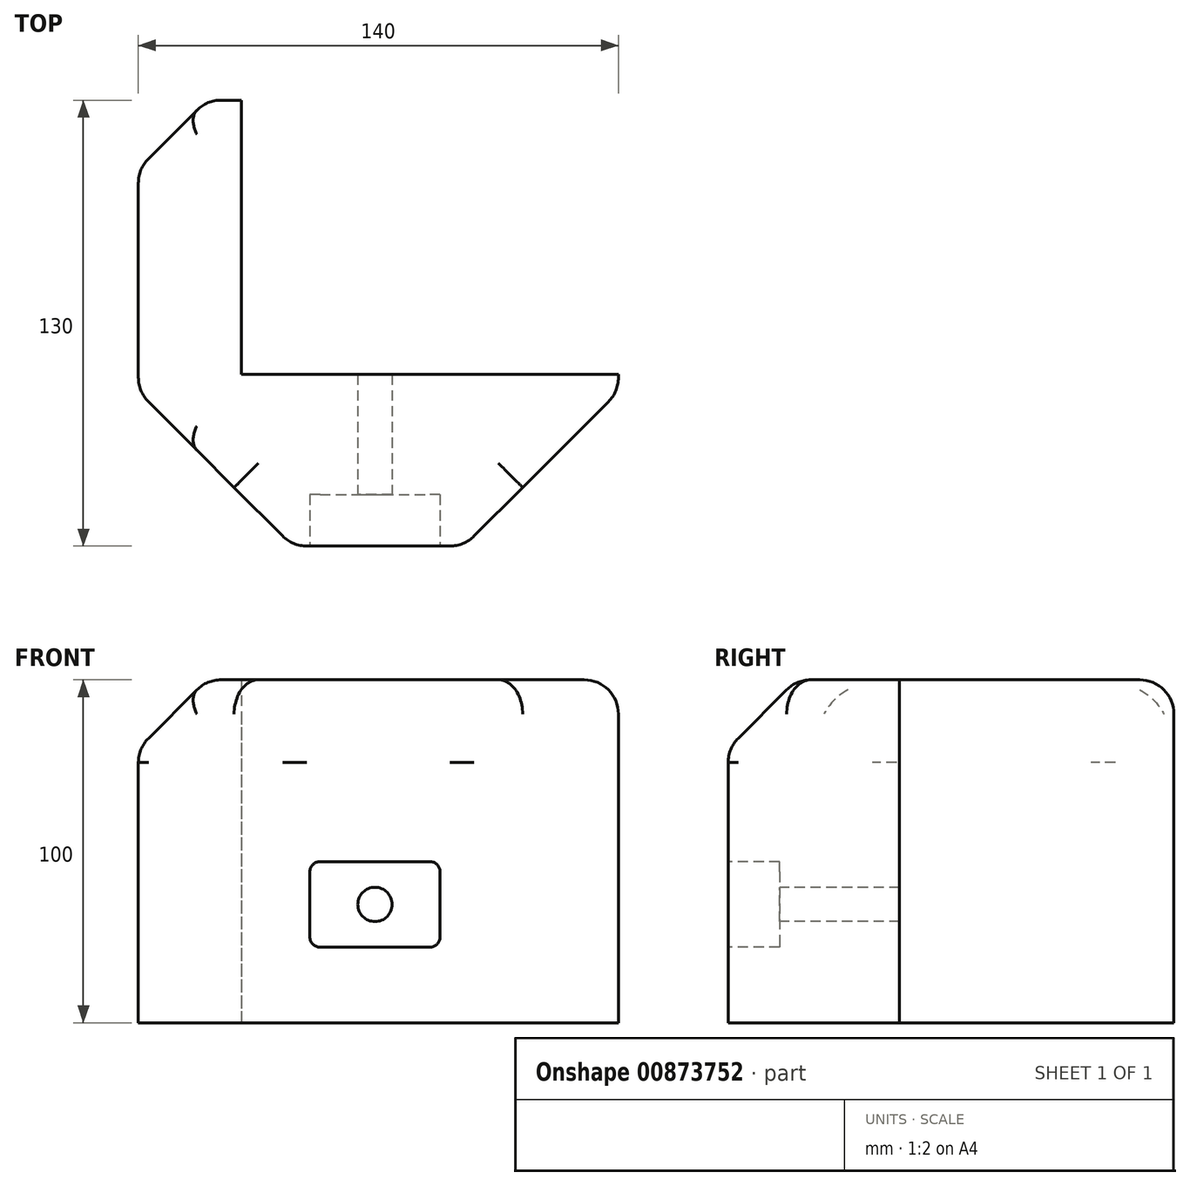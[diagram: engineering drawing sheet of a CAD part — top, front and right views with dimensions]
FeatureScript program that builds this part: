
annotation { "Feature Type Name" : "Feature", "Feature Type Description" : "" }
export const myFeature = defineFeature(function(context is Context, id is Id, definition is map)
    precondition{}
    {
        {
            var Q0;
            Q0=qCreatedBy(makeId("Top.planeOp"),FACE);
            var sketch = newSketch(context, id + "F0", { "sketchPlane" : qUnion([Q0])});
            skLineSegment(sketch, "E0.bottom", {"start": v(-91.77, 41.17) * mm, "end": v(48.23, 41.17) * mm});
            skLineSegment(sketch, "E0.top", {"start": v(-91.77, -8.83) * mm, "end": v(48.23, -8.83) * mm});
            skLineSegment(sketch, "E0.left", {"start": v(-91.77, 41.17) * mm, "end": v(-91.77, -8.83) * mm});
            skLineSegment(sketch, "E0.right", {"start": v(48.23, 41.17) * mm, "end": v(48.23, -8.83) * mm});
            skLineSegment(sketch, "E1.bottom", {"start": v(-91.77, 41.17) * mm, "end": v(-61.77, 41.17) * mm});
            skLineSegment(sketch, "E1.top", {"start": v(-91.77, 121.17) * mm, "end": v(-61.77, 121.17) * mm});
            skLineSegment(sketch, "E1.left", {"start": v(-91.77, 41.17) * mm, "end": v(-91.77, 121.17) * mm});
            skLineSegment(sketch, "E1.right", {"start": v(-61.77, 41.17) * mm, "end": v(-61.77, 121.17) * mm});
            skSolve(sketch);
        }
        {
            var Q0;
            Q0=makeQuery(id+"F0.imprint","IMPRINT",FACE,{"disambiguationData":[TD([[makeQuery(id+"F0.imprint","IMPRINT",EDGE,{"derivedFrom":sQuery(id+"F0.wireOp",EDGE,"E1.top")}),-1.0]])]});
            var Q1;
            Q1=makeQuery(id+"F0.imprint","IMPRINT",FACE,{"disambiguationData":[TD([[makeQuery(id+"F0.imprint","IMPRINT",EDGE,{"derivedFrom":sQuery(id+"F0.wireOp",EDGE,"E0.top")}),1.0]])]});
            extrude(context, id + "F1", {"entities" : qUnion([Q0, Q1]), "depth" : 100 * mm, "offsetDistance" : 25 * mm});
        }
        {
            var Q0;
            Q0=makeQuery(id+"F1.opExtrude","CAP_EDGE",EDGE,{"disambiguationData":[OSD([sQuery(id+"F0.wireOp",EDGE,"E0.top")])],"isStart":false});
            var Q1;
            Q1=makeQuery(id+"F1.opExtrude","CAP_EDGE",EDGE,{"disambiguationData":[OSD([sQuery(id+"F0.wireOp",EDGE,"E0.left"),sQuery(id+"F0.wireOp",EDGE,"E1.left")])],"isStart":false});
            chamfer(context, id + "F2", {"entities" : qUnion([Q0, Q1]), "width" : 20 * mm, "tangentPropagation" : true});
        }
        {
            var Q0;
            Q0=makeQuery(id+"F1.opExtrude","SWEPT_FACE",FACE,{"disambiguationData":[OSD([sQuery(id+"F0.wireOp",EDGE,"E0.top")])]});
            var sketch = newSketch(context, id + "F3", { "sketchPlane" : qUnion([Q0])});
            skLineSegment(sketch, "E2.bottom", {"start": v(-41.77, 47) * mm, "end": v(-3.77, 47) * mm});
            skLineSegment(sketch, "E2.top", {"start": v(-41.77, 22) * mm, "end": v(-3.77, 22) * mm});
            skLineSegment(sketch, "E2.left", {"start": v(-41.77, 47) * mm, "end": v(-41.77, 22) * mm});
            skLineSegment(sketch, "E2.right", {"start": v(-3.77, 47) * mm, "end": v(-3.77, 22) * mm});
            skSolve(sketch);
        }
        {
            var Q0;
            Q0 = qSketchRegion(id + "F3", true);
            extrude(context, id + "F4", {"entities" : qUnion([Q0]), "operationType" : NewBodyOperationType.REMOVE, "oppositeDirection" : true, "depth" : 15 * mm, "offsetDistance" : 25 * mm});
        }
        {
            var Q0;
            Q0=makeQuery(id+"F4.boolean.opBoolean","COPY",EDGE,{"derivedFrom":makeQuery(id+"F4.opExtrude","SWEPT_EDGE",EDGE,{"disambiguationData":[OSD([sQuery(id+"F3.wireOp",EDGE,"E2.bottom"),sQuery(id+"F3.wireOp",EDGE,"E2.left")])]})});
            var Q1;
            Q1=makeQuery(id+"F4.boolean.opBoolean","COPY",EDGE,{"derivedFrom":makeQuery(id+"F4.opExtrude","SWEPT_EDGE",EDGE,{"disambiguationData":[OSD([sQuery(id+"F3.wireOp",EDGE,"E2.top"),sQuery(id+"F3.wireOp",EDGE,"E2.left")])]})});
            var Q2;
            Q2=makeQuery(id+"F4.boolean.opBoolean","COPY",EDGE,{"derivedFrom":makeQuery(id+"F4.opExtrude","SWEPT_EDGE",EDGE,{"disambiguationData":[OSD([sQuery(id+"F3.wireOp",EDGE,"E2.top"),sQuery(id+"F3.wireOp",EDGE,"E2.right")])]})});
            var Q3;
            Q3=makeQuery(id+"F4.boolean.opBoolean","COPY",EDGE,{"derivedFrom":makeQuery(id+"F4.opExtrude","SWEPT_EDGE",EDGE,{"disambiguationData":[OSD([sQuery(id+"F3.wireOp",EDGE,"E2.bottom"),sQuery(id+"F3.wireOp",EDGE,"E2.right")])]})});
            fillet(context, id + "F5", {"entities" : qUnion([Q0, Q1, Q2, Q3]), "radius" : 3 * mm, "tangentPropagation" : true, "allowEdgeOverflow" : false});
        }
        {
            var Q0;
            Q0=makeQuery(id+"F1.opExtrude","SWEPT_EDGE",EDGE,{"disambiguationData":[OSD([sQuery(id+"F0.wireOp",EDGE,"E0.top"),sQuery(id+"F0.wireOp",EDGE,"E0.right")])]});
            var Q1;
            Q1=makeQuery(id+"F1.opExtrude","SWEPT_EDGE",EDGE,{"disambiguationData":[OSD([sQuery(id+"F0.wireOp",EDGE,"E0.top"),sQuery(id+"F0.wireOp",EDGE,"E0.left")])]});
            chamfer(context, id + "F6", {"entities" : qUnion([Q0, Q1]), "width" : 45 * mm, "tangentPropagation" : true});
        }
        {
            var Q0;
            Q0=makeQuery(id+"F1.opExtrude","SWEPT_EDGE",EDGE,{"disambiguationData":[OSD([sQuery(id+"F0.wireOp",EDGE,"E1.top"),sQuery(id+"F0.wireOp",EDGE,"E1.left")])]});
            chamfer(context, id + "F7", {"entities" : qUnion([Q0]), "width" : 20 * mm, "tangentPropagation" : true});
        }
        {
            var Q0;
            {var subQ0=sQuery(id+"F0.wireOp",EDGE,"E0.top");Q0=makeQuery(id+"F6.opChamfer","BLEND_EDGE",EDGE,{"blendedFrom":[makeQuery(id+"F1.opExtrude","SWEPT_EDGE",EDGE,{"disambiguationData":[OSD([subQ0,sQuery(id+"F0.wireOp",EDGE,"E0.left")])]}),makeQuery(id+"F1.opExtrude","SWEPT_FACE",FACE,{"disambiguationData":[OSD([subQ0])]})],"blendedInto":[makeQuery(id+"F1.opExtrude","SWEPT_FACE",FACE,{"disambiguationData":[OSD([subQ0])]})]});}
            var Q1;
            {var subQ0=sQuery(id+"F0.wireOp",EDGE,"E0.top");Q1=makeQuery(id+"F6.opChamfer","BLEND_EDGE",EDGE,{"blendedFrom":[makeQuery(id+"F1.opExtrude","SWEPT_EDGE",EDGE,{"disambiguationData":[OSD([subQ0,sQuery(id+"F0.wireOp",EDGE,"E0.right")])]}),makeQuery(id+"F1.opExtrude","SWEPT_FACE",FACE,{"disambiguationData":[OSD([subQ0])]})],"blendedInto":[makeQuery(id+"F1.opExtrude","SWEPT_FACE",FACE,{"disambiguationData":[OSD([subQ0])]})]});}
            var Q2;
            {var subQ0=sQuery(id+"F0.wireOp",EDGE,"E0.right");Q2=makeQuery(id+"F6.opChamfer","BLEND_EDGE",EDGE,{"blendedFrom":[makeQuery(id+"F1.opExtrude","SWEPT_EDGE",EDGE,{"disambiguationData":[OSD([sQuery(id+"F0.wireOp",EDGE,"E0.top"),subQ0])]}),makeQuery(id+"F1.opExtrude","SWEPT_FACE",FACE,{"disambiguationData":[OSD([subQ0])]})],"blendedInto":[makeQuery(id+"F1.opExtrude","SWEPT_FACE",FACE,{"disambiguationData":[OSD([subQ0])]})]});}
            var Q3;
            {var subQ0=sQuery(id+"F0.wireOp",EDGE,"E0.left");Q3=makeQuery(id+"F6.opChamfer","BLEND_EDGE",EDGE,{"blendedFrom":[makeQuery(id+"F1.opExtrude","SWEPT_EDGE",EDGE,{"disambiguationData":[OSD([sQuery(id+"F0.wireOp",EDGE,"E0.top"),subQ0])]}),makeQuery(id+"F1.opExtrude","SWEPT_FACE",FACE,{"disambiguationData":[OSD([subQ0,sQuery(id+"F0.wireOp",EDGE,"E1.left")])]})],"blendedInto":[makeQuery(id+"F1.opExtrude","SWEPT_FACE",FACE,{"disambiguationData":[OSD([subQ0,sQuery(id+"F0.wireOp",EDGE,"E1.left")])]})]});}
            var Q4;
            {var subQ0=sQuery(id+"F0.wireOp",EDGE,"E1.left");Q4=makeQuery(id+"F7.opChamfer","BLEND_EDGE",EDGE,{"blendedFrom":[makeQuery(id+"F1.opExtrude","SWEPT_EDGE",EDGE,{"disambiguationData":[OSD([sQuery(id+"F0.wireOp",EDGE,"E1.top"),subQ0])]}),makeQuery(id+"F1.opExtrude","SWEPT_FACE",FACE,{"disambiguationData":[OSD([sQuery(id+"F0.wireOp",EDGE,"E0.left"),subQ0])]})],"blendedInto":[makeQuery(id+"F1.opExtrude","SWEPT_FACE",FACE,{"disambiguationData":[OSD([sQuery(id+"F0.wireOp",EDGE,"E0.left"),subQ0])]})]});}
            var Q5;
            {var subQ0=sQuery(id+"F0.wireOp",EDGE,"E1.top");Q5=makeQuery(id+"F7.opChamfer","BLEND_EDGE",EDGE,{"blendedFrom":[makeQuery(id+"F1.opExtrude","SWEPT_EDGE",EDGE,{"disambiguationData":[OSD([subQ0,sQuery(id+"F0.wireOp",EDGE,"E1.left")])]}),makeQuery(id+"F1.opExtrude","SWEPT_FACE",FACE,{"disambiguationData":[OSD([subQ0])]})],"blendedInto":[makeQuery(id+"F1.opExtrude","SWEPT_FACE",FACE,{"disambiguationData":[OSD([subQ0])]})]});}
            fillet(context, id + "F8", {"entities" : qUnion([Q0, Q1, Q2, Q3, Q4, Q5]), "radius" : 10 * mm, "tangentPropagation" : true, "allowEdgeOverflow" : false});
        }
        {
            var Q0;
            Q0=makeQuery(id+"F4.boolean.opBoolean","COPY",FACE,{"derivedFrom":makeQuery(id+"F4.opExtrude","CAP_FACE",FACE,{"disambiguationData":[OSD([sQuery(id+"F3.wireOp",EDGE,"E2.bottom"),sQuery(id+"F3.wireOp",EDGE,"E2.top"),sQuery(id+"F3.wireOp",EDGE,"E2.left"),sQuery(id+"F3.wireOp",EDGE,"E2.right")])],"isStart":false})});
            var sketch = newSketch(context, id + "F9", { "sketchPlane" : qUnion([Q0])});
            skLineSegment(sketch, "E3", {"start": v(-38.77, 47) * mm, "end": v(-6.77, 22) * mm});
            skPoint(sketch, "E4", {"position": v(-22.77, 34.5) * mm});
            skCircle(sketch, "E5", {"center": v(-22.77, 34.5) * mm, "radius": 5 * mm});
            skSolve(sketch);
        }
        {
            var Q0;
            Q0 = qSketchRegion(id + "F9", true);
            extrude(context, id + "F10", {"entities" : qUnion([Q0]), "operationType" : NewBodyOperationType.REMOVE, "oppositeDirection" : true, "depth" : 80 * mm, "offsetDistance" : 25 * mm});
        }
        {
            var Q0;
            {var subQ0=sQuery(id+"F0.wireOp",EDGE,"E0.left");var subQ1=sQuery(id+"F0.wireOp",EDGE,"E0.top");Q0=makeQuery(id+"F6.opChamfer","BLEND_EDGE",EDGE,{"blendedFrom":[makeQuery(id+"F1.opExtrude","SWEPT_EDGE",EDGE,{"disambiguationData":[OSD([subQ1,subQ0])]}),makeQuery(id+"F1.opExtrude","CAP_FACE",FACE,{"disambiguationData":[OSD([sQuery(id+"F0.wireOp",EDGE,"E0.bottom"),subQ1,subQ0,sQuery(id+"F0.wireOp",EDGE,"E0.right"),sQuery(id+"F0.wireOp",EDGE,"E1.top"),sQuery(id+"F0.wireOp",EDGE,"E1.left"),sQuery(id+"F0.wireOp",EDGE,"E1.right")])],"isStart":false})],"blendedInto":[makeQuery(id+"F1.opExtrude","CAP_FACE",FACE,{"disambiguationData":[OSD([sQuery(id+"F0.wireOp",EDGE,"E0.bottom"),subQ1,subQ0,sQuery(id+"F0.wireOp",EDGE,"E0.right"),sQuery(id+"F0.wireOp",EDGE,"E1.top"),sQuery(id+"F0.wireOp",EDGE,"E1.left"),sQuery(id+"F0.wireOp",EDGE,"E1.right")])],"isStart":false})]});}
            var Q1;
            {var subQ0=sQuery(id+"F0.wireOp",EDGE,"E0.top");Q1=makeQuery(id+"F2.opChamfer","BLEND_EDGE",EDGE,{"blendedFrom":[makeQuery(id+"F1.opExtrude","CAP_EDGE",EDGE,{"disambiguationData":[OSD([subQ0])],"isStart":false}),makeQuery(id+"F1.opExtrude","SWEPT_FACE",FACE,{"disambiguationData":[OSD([subQ0])]})],"blendedInto":[makeQuery(id+"F1.opExtrude","SWEPT_FACE",FACE,{"disambiguationData":[OSD([subQ0])]})]});}
            var Q2;
            {var subQ0=sQuery(id+"F0.wireOp",EDGE,"E0.top");Q2=makeQuery(id+"F2.opChamfer","BLEND_EDGE",EDGE,{"blendedFrom":[makeQuery(id+"F1.opExtrude","CAP_EDGE",EDGE,{"disambiguationData":[OSD([subQ0])],"isStart":false}),makeQuery(id+"F1.opExtrude","CAP_FACE",FACE,{"disambiguationData":[OSD([sQuery(id+"F0.wireOp",EDGE,"E0.bottom"),subQ0,sQuery(id+"F0.wireOp",EDGE,"E0.left"),sQuery(id+"F0.wireOp",EDGE,"E0.right"),sQuery(id+"F0.wireOp",EDGE,"E1.top"),sQuery(id+"F0.wireOp",EDGE,"E1.left"),sQuery(id+"F0.wireOp",EDGE,"E1.right")])],"isStart":false})],"blendedInto":[makeQuery(id+"F1.opExtrude","CAP_FACE",FACE,{"disambiguationData":[OSD([sQuery(id+"F0.wireOp",EDGE,"E0.bottom"),subQ0,sQuery(id+"F0.wireOp",EDGE,"E0.left"),sQuery(id+"F0.wireOp",EDGE,"E0.right"),sQuery(id+"F0.wireOp",EDGE,"E1.top"),sQuery(id+"F0.wireOp",EDGE,"E1.left"),sQuery(id+"F0.wireOp",EDGE,"E1.right")])],"isStart":false})]});}
            var Q3;
            {var subQ0=sQuery(id+"F0.wireOp",EDGE,"E1.left");var subQ1=sQuery(id+"F0.wireOp",EDGE,"E0.left");Q3=makeQuery(id+"F2.opChamfer","BLEND_EDGE",EDGE,{"blendedFrom":[makeQuery(id+"F1.opExtrude","CAP_EDGE",EDGE,{"disambiguationData":[OSD([subQ1,subQ0])],"isStart":false}),makeQuery(id+"F1.opExtrude","CAP_FACE",FACE,{"disambiguationData":[OSD([sQuery(id+"F0.wireOp",EDGE,"E0.bottom"),sQuery(id+"F0.wireOp",EDGE,"E0.top"),subQ1,sQuery(id+"F0.wireOp",EDGE,"E0.right"),sQuery(id+"F0.wireOp",EDGE,"E1.top"),subQ0,sQuery(id+"F0.wireOp",EDGE,"E1.right")])],"isStart":false})],"blendedInto":[makeQuery(id+"F1.opExtrude","CAP_FACE",FACE,{"disambiguationData":[OSD([sQuery(id+"F0.wireOp",EDGE,"E0.bottom"),sQuery(id+"F0.wireOp",EDGE,"E0.top"),subQ1,sQuery(id+"F0.wireOp",EDGE,"E0.right"),sQuery(id+"F0.wireOp",EDGE,"E1.top"),subQ0,sQuery(id+"F0.wireOp",EDGE,"E1.right")])],"isStart":false})]});}
            var Q4;
            {var subQ0=sQuery(id+"F0.wireOp",EDGE,"E0.right");var subQ1=sQuery(id+"F0.wireOp",EDGE,"E0.top");Q4=makeQuery(id+"F6.opChamfer","BLEND_EDGE",EDGE,{"blendedFrom":[makeQuery(id+"F1.opExtrude","SWEPT_EDGE",EDGE,{"disambiguationData":[OSD([subQ1,subQ0])]}),makeQuery(id+"F1.opExtrude","CAP_FACE",FACE,{"disambiguationData":[OSD([sQuery(id+"F0.wireOp",EDGE,"E0.bottom"),subQ1,sQuery(id+"F0.wireOp",EDGE,"E0.left"),subQ0,sQuery(id+"F0.wireOp",EDGE,"E1.top"),sQuery(id+"F0.wireOp",EDGE,"E1.left"),sQuery(id+"F0.wireOp",EDGE,"E1.right")])],"isStart":false})],"blendedInto":[makeQuery(id+"F1.opExtrude","CAP_FACE",FACE,{"disambiguationData":[OSD([sQuery(id+"F0.wireOp",EDGE,"E0.bottom"),subQ1,sQuery(id+"F0.wireOp",EDGE,"E0.left"),subQ0,sQuery(id+"F0.wireOp",EDGE,"E1.top"),sQuery(id+"F0.wireOp",EDGE,"E1.left"),sQuery(id+"F0.wireOp",EDGE,"E1.right")])],"isStart":false})]});}
            fillet(context, id + "F11", {"entities" : qUnion([Q0, Q1, Q2, Q3, Q4]), "radius" : 10 * mm, "tangentPropagation" : true, "allowEdgeOverflow" : false});
        }
        {
            var Q0;
            {var subQ0=sQuery(id+"F0.wireOp",EDGE,"E1.left");var subQ1=sQuery(id+"F0.wireOp",EDGE,"E0.left");Q0=makeQuery(id+"F2.opChamfer","BLEND_EDGE",EDGE,{"blendedFrom":[makeQuery(id+"F1.opExtrude","CAP_EDGE",EDGE,{"disambiguationData":[OSD([subQ1,subQ0])],"isStart":false}),makeQuery(id+"F1.opExtrude","SWEPT_FACE",FACE,{"disambiguationData":[OSD([subQ1,subQ0])]})],"blendedInto":[makeQuery(id+"F1.opExtrude","SWEPT_FACE",FACE,{"disambiguationData":[OSD([subQ1,subQ0])]})]});}
            var Q1;
            {var subQ0=sQuery(id+"F0.wireOp",EDGE,"E0.left");Q1=makeQuery(id+"F6.opChamfer","BLEND_EDGE",EDGE,{"blendedFrom":[makeQuery(id+"F1.opExtrude","SWEPT_EDGE",EDGE,{"disambiguationData":[OSD([sQuery(id+"F0.wireOp",EDGE,"E0.top"),subQ0])]}),makeQuery(id+"F2.opChamfer","BLEND_FACE",FACE,{"disambiguationData":[OSD([subQ0,sQuery(id+"F0.wireOp",EDGE,"E1.left")])]})],"blendedInto":[makeQuery(id+"F2.opChamfer","BLEND_FACE",FACE,{"disambiguationData":[OSD([subQ0,sQuery(id+"F0.wireOp",EDGE,"E1.left")])]})]});}
            var Q2;
            {var subQ0=sQuery(id+"F0.wireOp",EDGE,"E1.left");Q2=makeQuery(id+"F7.opChamfer","BLEND_EDGE",EDGE,{"blendedFrom":[makeQuery(id+"F1.opExtrude","SWEPT_EDGE",EDGE,{"disambiguationData":[OSD([sQuery(id+"F0.wireOp",EDGE,"E1.top"),subQ0])]}),makeQuery(id+"F2.opChamfer","BLEND_FACE",FACE,{"disambiguationData":[OSD([sQuery(id+"F0.wireOp",EDGE,"E0.left"),subQ0])]})],"blendedInto":[makeQuery(id+"F2.opChamfer","BLEND_FACE",FACE,{"disambiguationData":[OSD([sQuery(id+"F0.wireOp",EDGE,"E0.left"),subQ0])]})]});}
            fillet(context, id + "F12", {"entities" : qUnion([Q0, Q1, Q2]), "radius" : 10 * mm, "tangentPropagation" : true, "allowEdgeOverflow" : false});
        }
    });
